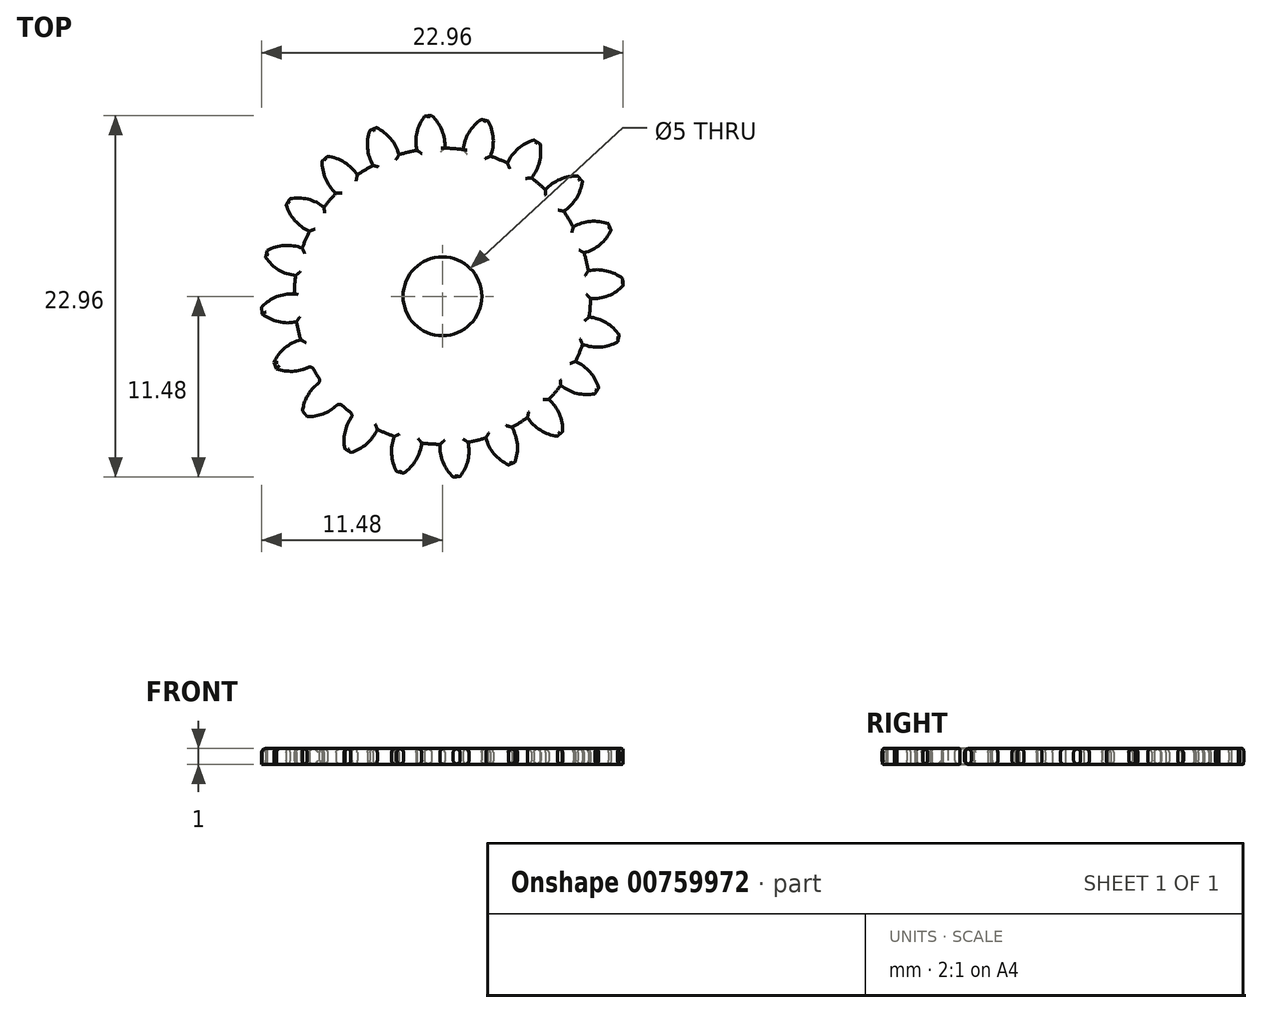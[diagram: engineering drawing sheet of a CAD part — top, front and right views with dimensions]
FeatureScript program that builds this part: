
annotation { "Feature Type Name" : "Feature", "Feature Type Description" : "" }
export const myFeature = defineFeature(function(context is Context, id is Id, definition is map)
    precondition{}
    {
        {
            assignVariable(context, id + "F0", {"name" : "GearDepth", "anyValue" : 1});
        }
        {
            assignVariable(context, id + "F1", {"name" : "TeethFillet", "anyValue" : getVariable(context, 'GearDepth') * .25});
        }
        {
            var Q0;
            Q0=qCreatedBy(makeId("Top.planeOp"),FACE);
            var sketch = newSketch(context, id + "F2", { "sketchPlane" : qUnion([Q0])});
            skCircle(sketch, "E0", {"center": v(0, 0) * mm, "radius": 9.4 * mm});
            skCircle(sketch, "E1", {"center": v(0, 0) * mm, "radius": 10.45 * mm, "construction": true});
            skCircle(sketch, "E2", {"center": v(0, 0) * mm, "radius": 11.5 * mm, "construction": true});
            skLineSegment(sketch, "E3", {"start": v(0, 0) * mm, "end": v(0, 17.6) * mm, "construction": true});
            skLineSegment(sketch, "E4", {"start": v(0, 0) * mm, "end": v(-1.42, 18) * mm, "construction": true});
            skLineSegment(sketch, "E5", {"start": v(0, 10.45) * mm, "end": v(-10.54, 10.45) * mm, "construction": true});
            skLineSegment(sketch, "E6", {"start": v(0, 10.45) * mm, "end": v(-10.3, 6.7) * mm, "construction": true});
            skCircle(sketch, "E7", {"center": v(0, 10.45) * mm, "radius": 2.61 * mm, "construction": true});
            skCircle(sketch, "E8", {"center": v(-2.46, 9.56) * mm, "radius": 2.61 * mm, "construction": true});
            skArc(sketch, "E9", {"start": v(-4.91, 10.45) * mm, "mid": v(-4.92, 10.42) * mm, "end": v(-4.94, 10.39) * mm});
            skArc(sketch, "E10.trimOffspring", {"start": v(0.15, 9.4) * mm, "mid": v(-0.03, 10.54) * mm, "end": v(-0.68, 11.48) * mm});
            skArc(sketch, "E11.MirrorCS", {"start": v(-1.62, 9.27) * mm, "mid": v(-1.62, 10.41) * mm, "end": v(-1.12, 11.45) * mm});
            skLineSegment(sketch, "E12", {"start": v(-1.12, 11.45) * mm, "end": v(-0.68, 11.48) * mm});
            skArc(sketch, "E13.1.0", {"start": v(-2.76, 9) * mm, "mid": v(-3.29, 10.01) * mm, "end": v(-4.2, 10.7) * mm});
            skLineSegment(sketch, "E13.1.1", {"start": v(-4.6, 10.54) * mm, "end": v(-4.2, 10.7) * mm});
            skArc(sketch, "E13.1.2", {"start": v(-4.4, 8.31) * mm, "mid": v(-4.76, 9.4) * mm, "end": v(-4.6, 10.54) * mm});
            skArc(sketch, "E13.2.0", {"start": v(-5.4, 7.7) * mm, "mid": v(-6.22, 8.5) * mm, "end": v(-7.3, 8.89) * mm});
            skLineSegment(sketch, "E13.2.1", {"start": v(-7.64, 8.6) * mm, "end": v(-7.3, 8.89) * mm});
            skArc(sketch, "E13.2.2", {"start": v(-6.76, 6.54) * mm, "mid": v(-7.43, 7.47) * mm, "end": v(-7.64, 8.6) * mm});
            skArc(sketch, "E13.3.0", {"start": v(-7.52, 5.65) * mm, "mid": v(-8.54, 6.17) * mm, "end": v(-9.69, 6.2) * mm});
            skLineSegment(sketch, "E13.3.1", {"start": v(-9.92, 5.82) * mm, "end": v(-9.69, 6.2) * mm});
            skArc(sketch, "E13.3.2", {"start": v(-8.45, 4.13) * mm, "mid": v(-9.37, 4.81) * mm, "end": v(-9.92, 5.82) * mm});
            skArc(sketch, "E13.4.0", {"start": v(-8.9, 3.05) * mm, "mid": v(-10.03, 3.23) * mm, "end": v(-11.13, 2.9) * mm});
            skLineSegment(sketch, "E13.4.1", {"start": v(-11.23, 2.47) * mm, "end": v(-11.13, 2.9) * mm});
            skArc(sketch, "E13.4.2", {"start": v(-9.32, 1.32) * mm, "mid": v(-10.4, 1.68) * mm, "end": v(-11.23, 2.47) * mm});
            skArc(sketch, "E13.5.0", {"start": v(-9.4, 0.15) * mm, "mid": v(-10.54, -0.03) * mm, "end": v(-11.48, -0.68) * mm});
            skLineSegment(sketch, "E13.5.1", {"start": v(-11.45, -1.12) * mm, "end": v(-11.48, -0.68) * mm});
            skArc(sketch, "E13.5.2", {"start": v(-9.27, -1.62) * mm, "mid": v(-10.41, -1.62) * mm, "end": v(-11.45, -1.12) * mm});
            skArc(sketch, "E13.6.0", {"start": v(-9, -2.76) * mm, "mid": v(-10.01, -3.29) * mm, "end": v(-10.7, -4.2) * mm});
            skLineSegment(sketch, "E13.6.1", {"start": v(-10.54, -4.6) * mm, "end": v(-10.7, -4.2) * mm});
            skArc(sketch, "E13.6.2", {"start": v(-8.31, -4.4) * mm, "mid": v(-9.4, -4.76) * mm, "end": v(-10.54, -4.6) * mm});
            skArc(sketch, "E13.7.0", {"start": v(-7.7, -5.4) * mm, "mid": v(-8.5, -6.22) * mm, "end": v(-8.89, -7.3) * mm});
            skLineSegment(sketch, "E13.7.1", {"start": v(-8.6, -7.64) * mm, "end": v(-8.89, -7.3) * mm});
            skArc(sketch, "E13.7.2", {"start": v(-6.54, -6.76) * mm, "mid": v(-7.47, -7.43) * mm, "end": v(-8.6, -7.64) * mm});
            skArc(sketch, "E13.8.0", {"start": v(-5.65, -7.52) * mm, "mid": v(-6.17, -8.54) * mm, "end": v(-6.2, -9.69) * mm});
            skLineSegment(sketch, "E13.8.1", {"start": v(-5.82, -9.92) * mm, "end": v(-6.2, -9.69) * mm});
            skArc(sketch, "E13.8.2", {"start": v(-4.13, -8.45) * mm, "mid": v(-4.81, -9.37) * mm, "end": v(-5.82, -9.92) * mm});
            skArc(sketch, "E13.9.0", {"start": v(-3.05, -8.9) * mm, "mid": v(-3.23, -10.03) * mm, "end": v(-2.9, -11.13) * mm});
            skLineSegment(sketch, "E13.9.1", {"start": v(-2.47, -11.23) * mm, "end": v(-2.9, -11.13) * mm});
            skArc(sketch, "E13.9.2", {"start": v(-1.32, -9.32) * mm, "mid": v(-1.68, -10.4) * mm, "end": v(-2.47, -11.23) * mm});
            skArc(sketch, "E13.10.0", {"start": v(-0.15, -9.4) * mm, "mid": v(0.03, -10.54) * mm, "end": v(0.68, -11.48) * mm});
            skLineSegment(sketch, "E13.10.1", {"start": v(1.12, -11.45) * mm, "end": v(0.68, -11.48) * mm});
            skArc(sketch, "E13.10.2", {"start": v(1.62, -9.27) * mm, "mid": v(1.62, -10.41) * mm, "end": v(1.12, -11.45) * mm});
            skArc(sketch, "E13.11.0", {"start": v(2.76, -9) * mm, "mid": v(3.29, -10.01) * mm, "end": v(4.2, -10.7) * mm});
            skLineSegment(sketch, "E13.11.1", {"start": v(4.6, -10.54) * mm, "end": v(4.2, -10.7) * mm});
            skArc(sketch, "E13.11.2", {"start": v(4.4, -8.31) * mm, "mid": v(4.76, -9.4) * mm, "end": v(4.6, -10.54) * mm});
            skArc(sketch, "E13.12.0", {"start": v(5.4, -7.7) * mm, "mid": v(6.22, -8.5) * mm, "end": v(7.3, -8.89) * mm});
            skLineSegment(sketch, "E13.12.1", {"start": v(7.64, -8.6) * mm, "end": v(7.3, -8.89) * mm});
            skArc(sketch, "E13.12.2", {"start": v(6.76, -6.54) * mm, "mid": v(7.43, -7.47) * mm, "end": v(7.64, -8.6) * mm});
            skArc(sketch, "E13.13.0", {"start": v(7.52, -5.65) * mm, "mid": v(8.54, -6.17) * mm, "end": v(9.69, -6.2) * mm});
            skLineSegment(sketch, "E13.13.1", {"start": v(9.92, -5.82) * mm, "end": v(9.69, -6.2) * mm});
            skArc(sketch, "E13.13.2", {"start": v(8.45, -4.13) * mm, "mid": v(9.37, -4.81) * mm, "end": v(9.92, -5.82) * mm});
            skArc(sketch, "E13.14.0", {"start": v(8.9, -3.05) * mm, "mid": v(10.03, -3.23) * mm, "end": v(11.13, -2.9) * mm});
            skLineSegment(sketch, "E13.14.1", {"start": v(11.23, -2.47) * mm, "end": v(11.13, -2.9) * mm});
            skArc(sketch, "E13.14.2", {"start": v(9.32, -1.32) * mm, "mid": v(10.4, -1.68) * mm, "end": v(11.23, -2.47) * mm});
            skArc(sketch, "E13.15.0", {"start": v(9.4, -0.15) * mm, "mid": v(10.54, 0.03) * mm, "end": v(11.48, 0.68) * mm});
            skLineSegment(sketch, "E13.15.1", {"start": v(11.45, 1.12) * mm, "end": v(11.48, 0.68) * mm});
            skArc(sketch, "E13.15.2", {"start": v(9.27, 1.62) * mm, "mid": v(10.41, 1.62) * mm, "end": v(11.45, 1.12) * mm});
            skArc(sketch, "E13.16.0", {"start": v(9, 2.76) * mm, "mid": v(10.01, 3.29) * mm, "end": v(10.7, 4.2) * mm});
            skLineSegment(sketch, "E13.16.1", {"start": v(10.54, 4.6) * mm, "end": v(10.7, 4.2) * mm});
            skArc(sketch, "E13.16.2", {"start": v(8.31, 4.4) * mm, "mid": v(9.4, 4.76) * mm, "end": v(10.54, 4.6) * mm});
            skArc(sketch, "E13.17.0", {"start": v(7.7, 5.4) * mm, "mid": v(8.5, 6.22) * mm, "end": v(8.89, 7.3) * mm});
            skLineSegment(sketch, "E13.17.1", {"start": v(8.6, 7.64) * mm, "end": v(8.89, 7.3) * mm});
            skArc(sketch, "E13.17.2", {"start": v(6.54, 6.76) * mm, "mid": v(7.47, 7.43) * mm, "end": v(8.6, 7.64) * mm});
            skArc(sketch, "E13.18.0", {"start": v(5.65, 7.52) * mm, "mid": v(6.17, 8.54) * mm, "end": v(6.2, 9.69) * mm});
            skLineSegment(sketch, "E13.18.1", {"start": v(5.82, 9.92) * mm, "end": v(6.2, 9.69) * mm});
            skArc(sketch, "E13.18.2", {"start": v(4.13, 8.45) * mm, "mid": v(4.81, 9.37) * mm, "end": v(5.82, 9.92) * mm});
            skArc(sketch, "E13.19.0", {"start": v(3.05, 8.9) * mm, "mid": v(3.23, 10.03) * mm, "end": v(2.9, 11.13) * mm});
            skLineSegment(sketch, "E13.19.1", {"start": v(2.47, 11.23) * mm, "end": v(2.9, 11.13) * mm});
            skArc(sketch, "E13.19.2", {"start": v(1.32, 9.32) * mm, "mid": v(1.68, 10.4) * mm, "end": v(2.47, 11.23) * mm});
            skCircle(sketch, "E14", {"center": v(0, 0) * mm, "radius": 2.5 * mm});
            skSolve(sketch);
        }
        {
            var Q0;
            {var subQ0=sQuery(id+"F2.wireOp",EDGE,"E10.trimOffspring");Q0=makeQuery(id+"F2.imprint","IMPRINT",FACE,{"disambiguationData":[TD([[makeQuery(id+"F2.imprint","IMPRINT",EDGE,{"derivedFrom":subQ0}),1.0]])]});}
            var Q1;
            {var subQ0=sQuery(id+"F2.wireOp",EDGE,"E0");var subQ1=makeQuery(id+"F2.imprint","INTERSECT",VERTEX,{"derivedFrom":[subQ0,sQuery(id+"F2.wireOp",EDGE,"E10.trimOffspring")]});Q1=makeQuery(id+"F2.imprint","IMPRINT",FACE,{"disambiguationData":[TD([[makeQuery(id+"F2.imprint","IMPRINT",EDGE,{"disambiguationData":[TD([[subQ1,-1.0]])],"derivedFrom":subQ0}),1.0]])]});}
            var Q2;
            {var subQ0=sQuery(id+"F2.wireOp",EDGE,"E13.1.0");Q2=makeQuery(id+"F2.imprint","IMPRINT",FACE,{"disambiguationData":[TD([[makeQuery(id+"F2.imprint","IMPRINT",EDGE,{"derivedFrom":subQ0}),1.0]])]});}
            var Q3;
            {var subQ0=sQuery(id+"F2.wireOp",EDGE,"E13.2.0");Q3=makeQuery(id+"F2.imprint","IMPRINT",FACE,{"disambiguationData":[TD([[makeQuery(id+"F2.imprint","IMPRINT",EDGE,{"derivedFrom":subQ0}),1.0]])]});}
            var Q4;
            {var subQ0=sQuery(id+"F2.wireOp",EDGE,"E13.3.0");Q4=makeQuery(id+"F2.imprint","IMPRINT",FACE,{"disambiguationData":[TD([[makeQuery(id+"F2.imprint","IMPRINT",EDGE,{"derivedFrom":subQ0}),1.0]])]});}
            var Q5;
            {var subQ0=sQuery(id+"F2.wireOp",EDGE,"E13.4.0");Q5=makeQuery(id+"F2.imprint","IMPRINT",FACE,{"disambiguationData":[TD([[makeQuery(id+"F2.imprint","IMPRINT",EDGE,{"derivedFrom":subQ0}),1.0]])]});}
            var Q6;
            {var subQ0=sQuery(id+"F2.wireOp",EDGE,"E13.5.0");Q6=makeQuery(id+"F2.imprint","IMPRINT",FACE,{"disambiguationData":[TD([[makeQuery(id+"F2.imprint","IMPRINT",EDGE,{"derivedFrom":subQ0}),1.0]])]});}
            var Q7;
            {var subQ0=sQuery(id+"F2.wireOp",EDGE,"E13.6.0");Q7=makeQuery(id+"F2.imprint","IMPRINT",FACE,{"disambiguationData":[TD([[makeQuery(id+"F2.imprint","IMPRINT",EDGE,{"derivedFrom":subQ0}),1.0]])]});}
            var Q8;
            {var subQ0=sQuery(id+"F2.wireOp",EDGE,"E13.7.0");Q8=makeQuery(id+"F2.imprint","IMPRINT",FACE,{"disambiguationData":[TD([[makeQuery(id+"F2.imprint","IMPRINT",EDGE,{"derivedFrom":subQ0}),1.0]])]});}
            var Q9;
            {var subQ0=sQuery(id+"F2.wireOp",EDGE,"E13.8.0");Q9=makeQuery(id+"F2.imprint","IMPRINT",FACE,{"disambiguationData":[TD([[makeQuery(id+"F2.imprint","IMPRINT",EDGE,{"derivedFrom":subQ0}),1.0]])]});}
            var Q10;
            {var subQ0=sQuery(id+"F2.wireOp",EDGE,"E13.9.0");Q10=makeQuery(id+"F2.imprint","IMPRINT",FACE,{"disambiguationData":[TD([[makeQuery(id+"F2.imprint","IMPRINT",EDGE,{"derivedFrom":subQ0}),1.0]])]});}
            var Q11;
            {var subQ0=sQuery(id+"F2.wireOp",EDGE,"E13.10.0");Q11=makeQuery(id+"F2.imprint","IMPRINT",FACE,{"disambiguationData":[TD([[makeQuery(id+"F2.imprint","IMPRINT",EDGE,{"derivedFrom":subQ0}),1.0]])]});}
            var Q12;
            {var subQ0=sQuery(id+"F2.wireOp",EDGE,"E13.11.0");Q12=makeQuery(id+"F2.imprint","IMPRINT",FACE,{"disambiguationData":[TD([[makeQuery(id+"F2.imprint","IMPRINT",EDGE,{"derivedFrom":subQ0}),1.0]])]});}
            var Q13;
            {var subQ0=sQuery(id+"F2.wireOp",EDGE,"E13.12.0");Q13=makeQuery(id+"F2.imprint","IMPRINT",FACE,{"disambiguationData":[TD([[makeQuery(id+"F2.imprint","IMPRINT",EDGE,{"derivedFrom":subQ0}),1.0]])]});}
            var Q14;
            {var subQ0=sQuery(id+"F2.wireOp",EDGE,"E13.13.0");Q14=makeQuery(id+"F2.imprint","IMPRINT",FACE,{"disambiguationData":[TD([[makeQuery(id+"F2.imprint","IMPRINT",EDGE,{"derivedFrom":subQ0}),1.0]])]});}
            var Q15;
            {var subQ0=sQuery(id+"F2.wireOp",EDGE,"E13.14.0");Q15=makeQuery(id+"F2.imprint","IMPRINT",FACE,{"disambiguationData":[TD([[makeQuery(id+"F2.imprint","IMPRINT",EDGE,{"derivedFrom":subQ0}),1.0]])]});}
            var Q16;
            {var subQ0=sQuery(id+"F2.wireOp",EDGE,"E13.15.0");Q16=makeQuery(id+"F2.imprint","IMPRINT",FACE,{"disambiguationData":[TD([[makeQuery(id+"F2.imprint","IMPRINT",EDGE,{"derivedFrom":subQ0}),1.0]])]});}
            var Q17;
            {var subQ0=sQuery(id+"F2.wireOp",EDGE,"E13.16.0");Q17=makeQuery(id+"F2.imprint","IMPRINT",FACE,{"disambiguationData":[TD([[makeQuery(id+"F2.imprint","IMPRINT",EDGE,{"derivedFrom":subQ0}),1.0]])]});}
            var Q18;
            {var subQ0=sQuery(id+"F2.wireOp",EDGE,"E13.17.0");Q18=makeQuery(id+"F2.imprint","IMPRINT",FACE,{"disambiguationData":[TD([[makeQuery(id+"F2.imprint","IMPRINT",EDGE,{"derivedFrom":subQ0}),1.0]])]});}
            var Q19;
            {var subQ0=sQuery(id+"F2.wireOp",EDGE,"E13.18.0");Q19=makeQuery(id+"F2.imprint","IMPRINT",FACE,{"disambiguationData":[TD([[makeQuery(id+"F2.imprint","IMPRINT",EDGE,{"derivedFrom":subQ0}),1.0]])]});}
            var Q20;
            {var subQ0=sQuery(id+"F2.wireOp",EDGE,"E13.19.0");Q20=makeQuery(id+"F2.imprint","IMPRINT",FACE,{"disambiguationData":[TD([[makeQuery(id+"F2.imprint","IMPRINT",EDGE,{"derivedFrom":subQ0}),1.0]])]});}
            var Q21;
            Q21=sQuery(id+"F2.wireOp",EDGE,"E0");
            var Q22;
            Q22=sQuery(id+"F2.wireOp",EDGE,"E10.trimOffspring");
            var Q23;
            Q23=sQuery(id+"F2.wireOp",EDGE,"E12");
            var Q24;
            Q24=sQuery(id+"F2.wireOp",EDGE,"E11.MirrorCS");
            extrude(context, id + "F3", {"entities" : qUnion([Q0, Q1, Q2, Q3, Q4, Q5, Q6, Q7, Q8, Q9, Q10, Q11, Q12, Q13, Q14, Q15, Q16, Q17, Q18, Q19, Q20]), "surfaceEntities" : qUnion([Q21, Q22, Q23, Q24]), "depth" : (getVariable(context, 'GearDepth')) * mm, "offsetDistance" : 25 * mm});
        }
        {
            var Q0;
            Q0=makeQuery(id+"F3.opExtrude","CAP_EDGE",EDGE,{"disambiguationData":[OSD([sQuery(id+"F2.wireOp",EDGE,"E13.5.2")])],"isStart":false});
            var Q1;
            Q1=makeQuery(id+"F3.opExtrude","CAP_EDGE",EDGE,{"disambiguationData":[OSD([sQuery(id+"F2.wireOp",EDGE,"E13.5.1")])],"isStart":false});
            var Q2;
            {var subQ0=sQuery(id+"F2.wireOp",EDGE,"E0");Q2=makeQuery(id+"F3.opExtrude","CAP_EDGE",EDGE,{"disambiguationData":[OSD([subQ0]),TDD([makeQuery(id+"F2.imprint","IMPRINT",EDGE,{"disambiguationData":[TD([[makeQuery(id+"F2.imprint","INTERSECT",VERTEX,{"derivedFrom":[subQ0,sQuery(id+"F2.wireOp",EDGE,"E13.5.2")]}),-1.0]])],"derivedFrom":subQ0})])],"isStart":false});}
            var Q3;
            Q3=makeQuery(id+"F3.opExtrude","CAP_EDGE",EDGE,{"disambiguationData":[OSD([sQuery(id+"F2.wireOp",EDGE,"E13.6.0")])],"isStart":false});
            var Q4;
            Q4=makeQuery(id+"F3.opExtrude","CAP_EDGE",EDGE,{"disambiguationData":[OSD([sQuery(id+"F2.wireOp",EDGE,"E13.6.1")])],"isStart":false});
            var Q5;
            Q5=makeQuery(id+"F3.opExtrude","CAP_EDGE",EDGE,{"disambiguationData":[OSD([sQuery(id+"F2.wireOp",EDGE,"E13.6.2")])],"isStart":false});
            var Q6;
            {var subQ0=sQuery(id+"F2.wireOp",EDGE,"E0");Q6=makeQuery(id+"F3.opExtrude","SWEPT_FACE",FACE,{"disambiguationData":[OSD([subQ0]),TDD([makeQuery(id+"F2.imprint","IMPRINT",EDGE,{"disambiguationData":[TD([[makeQuery(id+"F2.imprint","INTERSECT",VERTEX,{"derivedFrom":[subQ0,sQuery(id+"F2.wireOp",EDGE,"E13.6.2")]}),-1.0]])],"derivedFrom":subQ0})])]});}
            var Q7;
            {var subQ0=sQuery(id+"F2.wireOp",EDGE,"E0");Q7=makeQuery(id+"F3.opExtrude","CAP_EDGE",EDGE,{"disambiguationData":[OSD([subQ0]),TDD([makeQuery(id+"F2.imprint","IMPRINT",EDGE,{"disambiguationData":[TD([[makeQuery(id+"F2.imprint","INTERSECT",VERTEX,{"derivedFrom":[subQ0,sQuery(id+"F2.wireOp",EDGE,"E13.6.2")]}),-1.0]])],"derivedFrom":subQ0})])],"isStart":false});}
            var Q8;
            Q8=makeQuery(id+"F3.opExtrude","CAP_EDGE",EDGE,{"disambiguationData":[OSD([sQuery(id+"F2.wireOp",EDGE,"E13.7.2")])],"isStart":true});
            var Q9;
            {var subQ0=sQuery(id+"F2.wireOp",EDGE,"E0");Q9=makeQuery(id+"F3.opExtrude","CAP_EDGE",EDGE,{"disambiguationData":[OSD([subQ0]),TDD([makeQuery(id+"F2.imprint","IMPRINT",EDGE,{"disambiguationData":[TD([[makeQuery(id+"F2.imprint","INTERSECT",VERTEX,{"derivedFrom":[subQ0,sQuery(id+"F2.wireOp",EDGE,"E13.7.2")]}),-1.0]])],"derivedFrom":subQ0})])],"isStart":true});}
            var Q10;
            Q10=makeQuery(id+"F3.opExtrude","CAP_EDGE",EDGE,{"disambiguationData":[OSD([sQuery(id+"F2.wireOp",EDGE,"E13.7.2")])],"isStart":false});
            var Q11;
            {var subQ0=sQuery(id+"F2.wireOp",EDGE,"E0");Q11=makeQuery(id+"F3.opExtrude","CAP_EDGE",EDGE,{"disambiguationData":[OSD([subQ0]),TDD([makeQuery(id+"F2.imprint","IMPRINT",EDGE,{"disambiguationData":[TD([[makeQuery(id+"F2.imprint","INTERSECT",VERTEX,{"derivedFrom":[subQ0,sQuery(id+"F2.wireOp",EDGE,"E13.7.2")]}),-1.0]])],"derivedFrom":subQ0})])],"isStart":false});}
            var Q12;
            Q12=makeQuery(id+"F3.opExtrude","CAP_EDGE",EDGE,{"disambiguationData":[OSD([sQuery(id+"F2.wireOp",EDGE,"E13.8.0")])],"isStart":false});
            var Q13;
            {var subQ0=sQuery(id+"F2.wireOp",EDGE,"E0");Q13=makeQuery(id+"F3.opExtrude","SWEPT_FACE",FACE,{"disambiguationData":[OSD([subQ0]),TDD([makeQuery(id+"F2.imprint","IMPRINT",EDGE,{"disambiguationData":[TD([[makeQuery(id+"F2.imprint","INTERSECT",VERTEX,{"derivedFrom":[subQ0,sQuery(id+"F2.wireOp",EDGE,"E13.7.2")]}),-1.0]])],"derivedFrom":subQ0})])]});}
            var Q14;
            Q14=makeQuery(id+"F3.opExtrude","CAP_EDGE",EDGE,{"disambiguationData":[OSD([sQuery(id+"F2.wireOp",EDGE,"E13.6.0")])],"isStart":true});
            var Q15;
            Q15=makeQuery(id+"F3.opExtrude","CAP_EDGE",EDGE,{"disambiguationData":[OSD([sQuery(id+"F2.wireOp",EDGE,"E13.8.2")])],"isStart":false});
            var Q16;
            {var subQ0=sQuery(id+"F2.wireOp",EDGE,"E0");Q16=makeQuery(id+"F3.opExtrude","CAP_EDGE",EDGE,{"disambiguationData":[OSD([subQ0]),TDD([makeQuery(id+"F2.imprint","IMPRINT",EDGE,{"disambiguationData":[TD([[makeQuery(id+"F2.imprint","INTERSECT",VERTEX,{"derivedFrom":[subQ0,sQuery(id+"F2.wireOp",EDGE,"E13.8.2")]}),-1.0]])],"derivedFrom":subQ0})])],"isStart":false});}
            var Q17;
            Q17=makeQuery(id+"F3.opExtrude","CAP_EDGE",EDGE,{"disambiguationData":[OSD([sQuery(id+"F2.wireOp",EDGE,"E13.9.0")])],"isStart":false});
            var Q18;
            Q18=makeQuery(id+"F3.opExtrude","CAP_EDGE",EDGE,{"disambiguationData":[OSD([sQuery(id+"F2.wireOp",EDGE,"E13.9.2")])],"isStart":false});
            var Q19;
            {var subQ0=sQuery(id+"F2.wireOp",EDGE,"E0");Q19=makeQuery(id+"F3.opExtrude","CAP_EDGE",EDGE,{"disambiguationData":[OSD([subQ0]),TDD([makeQuery(id+"F2.imprint","IMPRINT",EDGE,{"disambiguationData":[TD([[makeQuery(id+"F2.imprint","INTERSECT",VERTEX,{"derivedFrom":[subQ0,sQuery(id+"F2.wireOp",EDGE,"E13.9.2")]}),-1.0]])],"derivedFrom":subQ0})])],"isStart":false});}
            var Q20;
            Q20=makeQuery(id+"F3.opExtrude","CAP_EDGE",EDGE,{"disambiguationData":[OSD([sQuery(id+"F2.wireOp",EDGE,"E13.10.0")])],"isStart":false});
            var Q21;
            Q21=makeQuery(id+"F3.opExtrude","CAP_EDGE",EDGE,{"disambiguationData":[OSD([sQuery(id+"F2.wireOp",EDGE,"E13.10.2")])],"isStart":false});
            var Q22;
            {var subQ0=sQuery(id+"F2.wireOp",EDGE,"E0");Q22=makeQuery(id+"F3.opExtrude","CAP_EDGE",EDGE,{"disambiguationData":[OSD([subQ0]),TDD([makeQuery(id+"F2.imprint","IMPRINT",EDGE,{"disambiguationData":[TD([[makeQuery(id+"F2.imprint","INTERSECT",VERTEX,{"derivedFrom":[subQ0,sQuery(id+"F2.wireOp",EDGE,"E13.10.2")]}),-1.0]])],"derivedFrom":subQ0})])],"isStart":false});}
            var Q23;
            Q23=makeQuery(id+"F3.opExtrude","CAP_EDGE",EDGE,{"disambiguationData":[OSD([sQuery(id+"F2.wireOp",EDGE,"E13.11.0")])],"isStart":false});
            var Q24;
            Q24=makeQuery(id+"F3.opExtrude","CAP_EDGE",EDGE,{"disambiguationData":[OSD([sQuery(id+"F2.wireOp",EDGE,"E13.11.2")])],"isStart":false});
            var Q25;
            {var subQ0=sQuery(id+"F2.wireOp",EDGE,"E0");Q25=makeQuery(id+"F3.opExtrude","CAP_EDGE",EDGE,{"disambiguationData":[OSD([subQ0]),TDD([makeQuery(id+"F2.imprint","IMPRINT",EDGE,{"disambiguationData":[TD([[makeQuery(id+"F2.imprint","INTERSECT",VERTEX,{"derivedFrom":[subQ0,sQuery(id+"F2.wireOp",EDGE,"E13.11.2")]}),-1.0]])],"derivedFrom":subQ0})])],"isStart":false});}
            var Q26;
            Q26=makeQuery(id+"F3.opExtrude","CAP_EDGE",EDGE,{"disambiguationData":[OSD([sQuery(id+"F2.wireOp",EDGE,"E13.12.0")])],"isStart":false});
            var Q27;
            Q27=makeQuery(id+"F3.opExtrude","CAP_EDGE",EDGE,{"disambiguationData":[OSD([sQuery(id+"F2.wireOp",EDGE,"E13.12.2")])],"isStart":false});
            var Q28;
            {var subQ0=sQuery(id+"F2.wireOp",EDGE,"E0");Q28=makeQuery(id+"F3.opExtrude","CAP_EDGE",EDGE,{"disambiguationData":[OSD([subQ0]),TDD([makeQuery(id+"F2.imprint","IMPRINT",EDGE,{"disambiguationData":[TD([[makeQuery(id+"F2.imprint","INTERSECT",VERTEX,{"derivedFrom":[subQ0,sQuery(id+"F2.wireOp",EDGE,"E13.12.2")]}),-1.0]])],"derivedFrom":subQ0})])],"isStart":false});}
            var Q29;
            Q29=makeQuery(id+"F3.opExtrude","CAP_EDGE",EDGE,{"disambiguationData":[OSD([sQuery(id+"F2.wireOp",EDGE,"E13.13.0")])],"isStart":false});
            var Q30;
            Q30=makeQuery(id+"F3.opExtrude","CAP_EDGE",EDGE,{"disambiguationData":[OSD([sQuery(id+"F2.wireOp",EDGE,"E13.13.2")])],"isStart":false});
            var Q31;
            {var subQ0=sQuery(id+"F2.wireOp",EDGE,"E0");Q31=makeQuery(id+"F3.opExtrude","CAP_EDGE",EDGE,{"disambiguationData":[OSD([subQ0]),TDD([makeQuery(id+"F2.imprint","IMPRINT",EDGE,{"disambiguationData":[TD([[makeQuery(id+"F2.imprint","INTERSECT",VERTEX,{"derivedFrom":[subQ0,sQuery(id+"F2.wireOp",EDGE,"E13.13.2")]}),-1.0]])],"derivedFrom":subQ0})])],"isStart":false});}
            var Q32;
            Q32=makeQuery(id+"F3.opExtrude","CAP_EDGE",EDGE,{"disambiguationData":[OSD([sQuery(id+"F2.wireOp",EDGE,"E13.14.0")])],"isStart":false});
            var Q33;
            Q33=makeQuery(id+"F3.opExtrude","CAP_EDGE",EDGE,{"disambiguationData":[OSD([sQuery(id+"F2.wireOp",EDGE,"E13.14.2")])],"isStart":false});
            var Q34;
            {var subQ0=sQuery(id+"F2.wireOp",EDGE,"E0");Q34=makeQuery(id+"F3.opExtrude","CAP_EDGE",EDGE,{"disambiguationData":[OSD([subQ0]),TDD([makeQuery(id+"F2.imprint","IMPRINT",EDGE,{"disambiguationData":[TD([[makeQuery(id+"F2.imprint","INTERSECT",VERTEX,{"derivedFrom":[subQ0,sQuery(id+"F2.wireOp",EDGE,"E13.14.2")]}),-1.0]])],"derivedFrom":subQ0})])],"isStart":false});}
            var Q35;
            Q35=makeQuery(id+"F3.opExtrude","CAP_EDGE",EDGE,{"disambiguationData":[OSD([sQuery(id+"F2.wireOp",EDGE,"E13.15.0")])],"isStart":false});
            var Q36;
            {var subQ0=sQuery(id+"F2.wireOp",EDGE,"E0");Q36=makeQuery(id+"F3.opExtrude","CAP_EDGE",EDGE,{"disambiguationData":[OSD([subQ0]),TDD([makeQuery(id+"F2.imprint","IMPRINT",EDGE,{"disambiguationData":[TD([[makeQuery(id+"F2.imprint","INTERSECT",VERTEX,{"derivedFrom":[subQ0,sQuery(id+"F2.wireOp",EDGE,"E13.14.2")]}),-1.0]])],"derivedFrom":subQ0})])],"isStart":false});}
            var Q37;
            Q37=makeQuery(id+"F3.opExtrude","CAP_EDGE",EDGE,{"disambiguationData":[OSD([sQuery(id+"F2.wireOp",EDGE,"E13.15.2")])],"isStart":false});
            var Q38;
            {var subQ0=sQuery(id+"F2.wireOp",EDGE,"E0");Q38=makeQuery(id+"F3.opExtrude","CAP_EDGE",EDGE,{"disambiguationData":[OSD([subQ0]),TDD([makeQuery(id+"F2.imprint","IMPRINT",EDGE,{"disambiguationData":[TD([[makeQuery(id+"F2.imprint","INTERSECT",VERTEX,{"derivedFrom":[subQ0,sQuery(id+"F2.wireOp",EDGE,"E13.15.2")]}),-1.0]])],"derivedFrom":subQ0})])],"isStart":false});}
            var Q39;
            Q39=makeQuery(id+"F3.opExtrude","CAP_EDGE",EDGE,{"disambiguationData":[OSD([sQuery(id+"F2.wireOp",EDGE,"E13.16.0")])],"isStart":false});
            var Q40;
            Q40=makeQuery(id+"F3.opExtrude","CAP_EDGE",EDGE,{"disambiguationData":[OSD([sQuery(id+"F2.wireOp",EDGE,"E13.16.2")])],"isStart":false});
            var Q41;
            Q41=makeQuery(id+"F3.opExtrude","CAP_EDGE",EDGE,{"disambiguationData":[OSD([sQuery(id+"F2.wireOp",EDGE,"E13.17.0")])],"isStart":false});
            var Q42;
            {var subQ0=sQuery(id+"F2.wireOp",EDGE,"E0");Q42=makeQuery(id+"F3.opExtrude","CAP_EDGE",EDGE,{"disambiguationData":[OSD([subQ0]),TDD([makeQuery(id+"F2.imprint","IMPRINT",EDGE,{"disambiguationData":[TD([[makeQuery(id+"F2.imprint","INTERSECT",VERTEX,{"derivedFrom":[subQ0,sQuery(id+"F2.wireOp",EDGE,"E13.16.2")]}),-1.0]])],"derivedFrom":subQ0})])],"isStart":false});}
            var Q43;
            Q43=makeQuery(id+"F3.opExtrude","CAP_EDGE",EDGE,{"disambiguationData":[OSD([sQuery(id+"F2.wireOp",EDGE,"E13.17.2")])],"isStart":false});
            var Q44;
            {var subQ0=sQuery(id+"F2.wireOp",EDGE,"E0");Q44=makeQuery(id+"F3.opExtrude","CAP_EDGE",EDGE,{"disambiguationData":[OSD([subQ0]),TDD([makeQuery(id+"F2.imprint","IMPRINT",EDGE,{"disambiguationData":[TD([[makeQuery(id+"F2.imprint","INTERSECT",VERTEX,{"derivedFrom":[subQ0,sQuery(id+"F2.wireOp",EDGE,"E13.17.2")]}),-1.0]])],"derivedFrom":subQ0})])],"isStart":false});}
            var Q45;
            Q45=makeQuery(id+"F3.opExtrude","CAP_EDGE",EDGE,{"disambiguationData":[OSD([sQuery(id+"F2.wireOp",EDGE,"E13.18.0")])],"isStart":false});
            var Q46;
            Q46=makeQuery(id+"F3.opExtrude","CAP_EDGE",EDGE,{"disambiguationData":[OSD([sQuery(id+"F2.wireOp",EDGE,"E13.18.2")])],"isStart":false});
            var Q47;
            {var subQ0=sQuery(id+"F2.wireOp",EDGE,"E0");Q47=makeQuery(id+"F3.opExtrude","CAP_EDGE",EDGE,{"disambiguationData":[OSD([subQ0]),TDD([makeQuery(id+"F2.imprint","IMPRINT",EDGE,{"disambiguationData":[TD([[makeQuery(id+"F2.imprint","INTERSECT",VERTEX,{"derivedFrom":[subQ0,sQuery(id+"F2.wireOp",EDGE,"E13.18.2")]}),-1.0]])],"derivedFrom":subQ0})])],"isStart":false});}
            var Q48;
            Q48=makeQuery(id+"F3.opExtrude","CAP_EDGE",EDGE,{"disambiguationData":[OSD([sQuery(id+"F2.wireOp",EDGE,"E13.19.0")])],"isStart":false});
            var Q49;
            Q49=makeQuery(id+"F3.opExtrude","CAP_EDGE",EDGE,{"disambiguationData":[OSD([sQuery(id+"F2.wireOp",EDGE,"E13.19.2")])],"isStart":false});
            var Q50;
            Q50=makeQuery(id+"F3.opExtrude","CAP_EDGE",EDGE,{"disambiguationData":[OSD([sQuery(id+"F2.wireOp",EDGE,"E10.trimOffspring")])],"isStart":false});
            var Q51;
            Q51=makeQuery(id+"F3.opExtrude","CAP_EDGE",EDGE,{"disambiguationData":[OSD([sQuery(id+"F2.wireOp",EDGE,"E11.MirrorCS")])],"isStart":false});
            var Q52;
            {var subQ0=sQuery(id+"F2.wireOp",EDGE,"E0");Q52=makeQuery(id+"F3.opExtrude","CAP_EDGE",EDGE,{"disambiguationData":[OSD([subQ0]),TDD([makeQuery(id+"F2.imprint","IMPRINT",EDGE,{"disambiguationData":[TD([[makeQuery(id+"F2.imprint","INTERSECT",VERTEX,{"derivedFrom":[subQ0,sQuery(id+"F2.wireOp",EDGE,"E11.MirrorCS")]}),-1.0]])],"derivedFrom":subQ0})])],"isStart":false});}
            var Q53;
            Q53=makeQuery(id+"F3.opExtrude","CAP_EDGE",EDGE,{"disambiguationData":[OSD([sQuery(id+"F2.wireOp",EDGE,"E13.1.0")])],"isStart":false});
            var Q54;
            Q54=makeQuery(id+"F3.opExtrude","CAP_EDGE",EDGE,{"disambiguationData":[OSD([sQuery(id+"F2.wireOp",EDGE,"E13.1.2")])],"isStart":false});
            var Q55;
            {var subQ0=sQuery(id+"F2.wireOp",EDGE,"E0");Q55=makeQuery(id+"F3.opExtrude","CAP_EDGE",EDGE,{"disambiguationData":[OSD([subQ0]),TDD([makeQuery(id+"F2.imprint","IMPRINT",EDGE,{"disambiguationData":[TD([[makeQuery(id+"F2.imprint","INTERSECT",VERTEX,{"derivedFrom":[subQ0,sQuery(id+"F2.wireOp",EDGE,"E13.1.2")]}),-1.0]])],"derivedFrom":subQ0})])],"isStart":false});}
            var Q56;
            Q56=makeQuery(id+"F3.opExtrude","CAP_EDGE",EDGE,{"disambiguationData":[OSD([sQuery(id+"F2.wireOp",EDGE,"E13.2.0")])],"isStart":false});
            var Q57;
            Q57=makeQuery(id+"F3.opExtrude","CAP_EDGE",EDGE,{"disambiguationData":[OSD([sQuery(id+"F2.wireOp",EDGE,"E13.2.2")])],"isStart":false});
            var Q58;
            {var subQ0=sQuery(id+"F2.wireOp",EDGE,"E0");Q58=makeQuery(id+"F3.opExtrude","CAP_EDGE",EDGE,{"disambiguationData":[OSD([subQ0]),TDD([makeQuery(id+"F2.imprint","IMPRINT",EDGE,{"disambiguationData":[TD([[makeQuery(id+"F2.imprint","INTERSECT",VERTEX,{"derivedFrom":[subQ0,sQuery(id+"F2.wireOp",EDGE,"E13.2.2")]}),-1.0]])],"derivedFrom":subQ0})])],"isStart":false});}
            var Q59;
            Q59=makeQuery(id+"F3.opExtrude","CAP_EDGE",EDGE,{"disambiguationData":[OSD([sQuery(id+"F2.wireOp",EDGE,"E13.3.0")])],"isStart":false});
            var Q60;
            Q60=makeQuery(id+"F3.opExtrude","CAP_EDGE",EDGE,{"disambiguationData":[OSD([sQuery(id+"F2.wireOp",EDGE,"E13.3.2")])],"isStart":false});
            var Q61;
            {var subQ0=sQuery(id+"F2.wireOp",EDGE,"E0");Q61=makeQuery(id+"F3.opExtrude","CAP_EDGE",EDGE,{"disambiguationData":[OSD([subQ0]),TDD([makeQuery(id+"F2.imprint","IMPRINT",EDGE,{"disambiguationData":[TD([[makeQuery(id+"F2.imprint","INTERSECT",VERTEX,{"derivedFrom":[subQ0,sQuery(id+"F2.wireOp",EDGE,"E13.3.2")]}),-1.0]])],"derivedFrom":subQ0})])],"isStart":false});}
            var Q62;
            Q62=makeQuery(id+"F3.opExtrude","CAP_EDGE",EDGE,{"disambiguationData":[OSD([sQuery(id+"F2.wireOp",EDGE,"E13.4.0")])],"isStart":false});
            var Q63;
            Q63=makeQuery(id+"F3.opExtrude","CAP_EDGE",EDGE,{"disambiguationData":[OSD([sQuery(id+"F2.wireOp",EDGE,"E13.4.2")])],"isStart":false});
            var Q64;
            {var subQ0=sQuery(id+"F2.wireOp",EDGE,"E0");Q64=makeQuery(id+"F3.opExtrude","CAP_EDGE",EDGE,{"disambiguationData":[OSD([subQ0]),TDD([makeQuery(id+"F2.imprint","IMPRINT",EDGE,{"disambiguationData":[TD([[makeQuery(id+"F2.imprint","INTERSECT",VERTEX,{"derivedFrom":[subQ0,sQuery(id+"F2.wireOp",EDGE,"E13.4.2")]}),-1.0]])],"derivedFrom":subQ0})])],"isStart":false});}
            var Q65;
            {var subQ0=sQuery(id+"F2.wireOp",EDGE,"E0");Q65=makeQuery(id+"F3.opExtrude","CAP_EDGE",EDGE,{"disambiguationData":[OSD([subQ0]),TDD([makeQuery(id+"F2.imprint","IMPRINT",EDGE,{"disambiguationData":[TD([[makeQuery(id+"F2.imprint","INTERSECT",VERTEX,{"derivedFrom":[subQ0,sQuery(id+"F2.wireOp",EDGE,"E13.5.2")]}),-1.0]])],"derivedFrom":subQ0})])],"isStart":true});}
            var Q66;
            Q66=makeQuery(id+"F3.opExtrude","CAP_EDGE",EDGE,{"disambiguationData":[OSD([sQuery(id+"F2.wireOp",EDGE,"E13.5.2")])],"isStart":true});
            var Q67;
            {var subQ0=sQuery(id+"F2.wireOp",EDGE,"E0");Q67=makeQuery(id+"F3.opExtrude","CAP_EDGE",EDGE,{"disambiguationData":[OSD([subQ0]),TDD([makeQuery(id+"F2.imprint","IMPRINT",EDGE,{"disambiguationData":[TD([[makeQuery(id+"F2.imprint","INTERSECT",VERTEX,{"derivedFrom":[subQ0,sQuery(id+"F2.wireOp",EDGE,"E13.4.2")]}),-1.0]])],"derivedFrom":subQ0})])],"isStart":true});}
            var Q68;
            Q68=makeQuery(id+"F3.opExtrude","CAP_EDGE",EDGE,{"disambiguationData":[OSD([sQuery(id+"F2.wireOp",EDGE,"E13.4.2")])],"isStart":true});
            var Q69;
            Q69=makeQuery(id+"F3.opExtrude","CAP_EDGE",EDGE,{"disambiguationData":[OSD([sQuery(id+"F2.wireOp",EDGE,"E13.4.0")])],"isStart":true});
            var Q70;
            {var subQ0=sQuery(id+"F2.wireOp",EDGE,"E0");Q70=makeQuery(id+"F3.opExtrude","CAP_EDGE",EDGE,{"disambiguationData":[OSD([subQ0]),TDD([makeQuery(id+"F2.imprint","IMPRINT",EDGE,{"disambiguationData":[TD([[makeQuery(id+"F2.imprint","INTERSECT",VERTEX,{"derivedFrom":[subQ0,sQuery(id+"F2.wireOp",EDGE,"E13.3.2")]}),-1.0]])],"derivedFrom":subQ0})])],"isStart":true});}
            var Q71;
            Q71=makeQuery(id+"F3.opExtrude","CAP_EDGE",EDGE,{"disambiguationData":[OSD([sQuery(id+"F2.wireOp",EDGE,"E13.3.2")])],"isStart":true});
            var Q72;
            Q72=makeQuery(id+"F3.opExtrude","CAP_EDGE",EDGE,{"disambiguationData":[OSD([sQuery(id+"F2.wireOp",EDGE,"E13.3.0")])],"isStart":true});
            var Q73;
            {var subQ0=sQuery(id+"F2.wireOp",EDGE,"E0");Q73=makeQuery(id+"F3.opExtrude","CAP_EDGE",EDGE,{"disambiguationData":[OSD([subQ0]),TDD([makeQuery(id+"F2.imprint","IMPRINT",EDGE,{"disambiguationData":[TD([[makeQuery(id+"F2.imprint","INTERSECT",VERTEX,{"derivedFrom":[subQ0,sQuery(id+"F2.wireOp",EDGE,"E13.2.2")]}),-1.0]])],"derivedFrom":subQ0})])],"isStart":true});}
            var Q74;
            Q74=makeQuery(id+"F3.opExtrude","CAP_EDGE",EDGE,{"disambiguationData":[OSD([sQuery(id+"F2.wireOp",EDGE,"E13.2.2")])],"isStart":true});
            var Q75;
            Q75=makeQuery(id+"F3.opExtrude","CAP_EDGE",EDGE,{"disambiguationData":[OSD([sQuery(id+"F2.wireOp",EDGE,"E13.2.0")])],"isStart":true});
            var Q76;
            Q76=makeQuery(id+"F3.opExtrude","CAP_EDGE",EDGE,{"disambiguationData":[OSD([sQuery(id+"F2.wireOp",EDGE,"E13.1.2")])],"isStart":true});
            var Q77;
            {var subQ0=sQuery(id+"F2.wireOp",EDGE,"E0");Q77=makeQuery(id+"F3.opExtrude","CAP_EDGE",EDGE,{"disambiguationData":[OSD([subQ0]),TDD([makeQuery(id+"F2.imprint","IMPRINT",EDGE,{"disambiguationData":[TD([[makeQuery(id+"F2.imprint","INTERSECT",VERTEX,{"derivedFrom":[subQ0,sQuery(id+"F2.wireOp",EDGE,"E13.1.2")]}),-1.0]])],"derivedFrom":subQ0})])],"isStart":true});}
            var Q78;
            Q78=makeQuery(id+"F3.opExtrude","CAP_EDGE",EDGE,{"disambiguationData":[OSD([sQuery(id+"F2.wireOp",EDGE,"E13.1.0")])],"isStart":true});
            var Q79;
            {var subQ0=sQuery(id+"F2.wireOp",EDGE,"E0");Q79=makeQuery(id+"F3.opExtrude","CAP_EDGE",EDGE,{"disambiguationData":[OSD([subQ0]),TDD([makeQuery(id+"F2.imprint","IMPRINT",EDGE,{"disambiguationData":[TD([[makeQuery(id+"F2.imprint","INTERSECT",VERTEX,{"derivedFrom":[subQ0,sQuery(id+"F2.wireOp",EDGE,"E11.MirrorCS")]}),-1.0]])],"derivedFrom":subQ0})])],"isStart":true});}
            var Q80;
            Q80=makeQuery(id+"F3.opExtrude","CAP_EDGE",EDGE,{"disambiguationData":[OSD([sQuery(id+"F2.wireOp",EDGE,"E11.MirrorCS")])],"isStart":true});
            var Q81;
            Q81=makeQuery(id+"F3.opExtrude","CAP_EDGE",EDGE,{"disambiguationData":[OSD([sQuery(id+"F2.wireOp",EDGE,"E10.trimOffspring")])],"isStart":true});
            var Q82;
            {var subQ0=sQuery(id+"F2.wireOp",EDGE,"E0");Q82=makeQuery(id+"F3.opExtrude","CAP_EDGE",EDGE,{"disambiguationData":[OSD([subQ0]),TDD([makeQuery(id+"F2.imprint","IMPRINT",EDGE,{"disambiguationData":[TD([[makeQuery(id+"F2.imprint","INTERSECT",VERTEX,{"derivedFrom":[subQ0,sQuery(id+"F2.wireOp",EDGE,"E10.trimOffspring")]}),1.0]])],"derivedFrom":subQ0})])],"isStart":true});}
            var Q83;
            Q83=makeQuery(id+"F3.opExtrude","CAP_EDGE",EDGE,{"disambiguationData":[OSD([sQuery(id+"F2.wireOp",EDGE,"E13.19.2")])],"isStart":true});
            var Q84;
            Q84=makeQuery(id+"F3.opExtrude","CAP_EDGE",EDGE,{"disambiguationData":[OSD([sQuery(id+"F2.wireOp",EDGE,"E13.19.0")])],"isStart":true});
            var Q85;
            {var subQ0=sQuery(id+"F2.wireOp",EDGE,"E0");Q85=makeQuery(id+"F3.opExtrude","CAP_EDGE",EDGE,{"disambiguationData":[OSD([subQ0]),TDD([makeQuery(id+"F2.imprint","IMPRINT",EDGE,{"disambiguationData":[TD([[makeQuery(id+"F2.imprint","INTERSECT",VERTEX,{"derivedFrom":[subQ0,sQuery(id+"F2.wireOp",EDGE,"E13.18.2")]}),-1.0]])],"derivedFrom":subQ0})])],"isStart":true});}
            var Q86;
            Q86=makeQuery(id+"F3.opExtrude","CAP_EDGE",EDGE,{"disambiguationData":[OSD([sQuery(id+"F2.wireOp",EDGE,"E13.18.2")])],"isStart":true});
            var Q87;
            Q87=makeQuery(id+"F3.opExtrude","CAP_EDGE",EDGE,{"disambiguationData":[OSD([sQuery(id+"F2.wireOp",EDGE,"E13.18.0")])],"isStart":true});
            var Q88;
            {var subQ0=sQuery(id+"F2.wireOp",EDGE,"E0");Q88=makeQuery(id+"F3.opExtrude","CAP_EDGE",EDGE,{"disambiguationData":[OSD([subQ0]),TDD([makeQuery(id+"F2.imprint","IMPRINT",EDGE,{"disambiguationData":[TD([[makeQuery(id+"F2.imprint","INTERSECT",VERTEX,{"derivedFrom":[subQ0,sQuery(id+"F2.wireOp",EDGE,"E13.17.2")]}),-1.0]])],"derivedFrom":subQ0})])],"isStart":true});}
            var Q89;
            Q89=makeQuery(id+"F3.opExtrude","CAP_EDGE",EDGE,{"disambiguationData":[OSD([sQuery(id+"F2.wireOp",EDGE,"E13.17.2")])],"isStart":true});
            var Q90;
            Q90=makeQuery(id+"F3.opExtrude","CAP_EDGE",EDGE,{"disambiguationData":[OSD([sQuery(id+"F2.wireOp",EDGE,"E13.17.0")])],"isStart":true});
            var Q91;
            {var subQ0=sQuery(id+"F2.wireOp",EDGE,"E0");Q91=makeQuery(id+"F3.opExtrude","CAP_EDGE",EDGE,{"disambiguationData":[OSD([subQ0]),TDD([makeQuery(id+"F2.imprint","IMPRINT",EDGE,{"disambiguationData":[TD([[makeQuery(id+"F2.imprint","INTERSECT",VERTEX,{"derivedFrom":[subQ0,sQuery(id+"F2.wireOp",EDGE,"E13.16.2")]}),-1.0]])],"derivedFrom":subQ0})])],"isStart":true});}
            var Q92;
            Q92=makeQuery(id+"F3.opExtrude","CAP_EDGE",EDGE,{"disambiguationData":[OSD([sQuery(id+"F2.wireOp",EDGE,"E13.16.2")])],"isStart":true});
            var Q93;
            Q93=makeQuery(id+"F3.opExtrude","CAP_EDGE",EDGE,{"disambiguationData":[OSD([sQuery(id+"F2.wireOp",EDGE,"E13.16.0")])],"isStart":true});
            var Q94;
            {var subQ0=sQuery(id+"F2.wireOp",EDGE,"E0");Q94=makeQuery(id+"F3.opExtrude","CAP_EDGE",EDGE,{"disambiguationData":[OSD([subQ0]),TDD([makeQuery(id+"F2.imprint","IMPRINT",EDGE,{"disambiguationData":[TD([[makeQuery(id+"F2.imprint","INTERSECT",VERTEX,{"derivedFrom":[subQ0,sQuery(id+"F2.wireOp",EDGE,"E13.15.2")]}),-1.0]])],"derivedFrom":subQ0})])],"isStart":true});}
            var Q95;
            Q95=makeQuery(id+"F3.opExtrude","CAP_EDGE",EDGE,{"disambiguationData":[OSD([sQuery(id+"F2.wireOp",EDGE,"E13.15.2")])],"isStart":true});
            var Q96;
            Q96=makeQuery(id+"F3.opExtrude","CAP_EDGE",EDGE,{"disambiguationData":[OSD([sQuery(id+"F2.wireOp",EDGE,"E13.15.0")])],"isStart":true});
            var Q97;
            {var subQ0=sQuery(id+"F2.wireOp",EDGE,"E0");Q97=makeQuery(id+"F3.opExtrude","CAP_EDGE",EDGE,{"disambiguationData":[OSD([subQ0]),TDD([makeQuery(id+"F2.imprint","IMPRINT",EDGE,{"disambiguationData":[TD([[makeQuery(id+"F2.imprint","INTERSECT",VERTEX,{"derivedFrom":[subQ0,sQuery(id+"F2.wireOp",EDGE,"E13.14.2")]}),-1.0]])],"derivedFrom":subQ0})])],"isStart":true});}
            var Q98;
            Q98=makeQuery(id+"F3.opExtrude","CAP_EDGE",EDGE,{"disambiguationData":[OSD([sQuery(id+"F2.wireOp",EDGE,"E13.14.2")])],"isStart":true});
            var Q99;
            Q99=makeQuery(id+"F3.opExtrude","CAP_EDGE",EDGE,{"disambiguationData":[OSD([sQuery(id+"F2.wireOp",EDGE,"E13.14.0")])],"isStart":true});
            var Q100;
            {var subQ0=sQuery(id+"F2.wireOp",EDGE,"E0");Q100=makeQuery(id+"F3.opExtrude","CAP_EDGE",EDGE,{"disambiguationData":[OSD([subQ0]),TDD([makeQuery(id+"F2.imprint","IMPRINT",EDGE,{"disambiguationData":[TD([[makeQuery(id+"F2.imprint","INTERSECT",VERTEX,{"derivedFrom":[subQ0,sQuery(id+"F2.wireOp",EDGE,"E13.13.2")]}),-1.0]])],"derivedFrom":subQ0})])],"isStart":true});}
            var Q101;
            Q101=makeQuery(id+"F3.opExtrude","CAP_EDGE",EDGE,{"disambiguationData":[OSD([sQuery(id+"F2.wireOp",EDGE,"E13.13.2")])],"isStart":true});
            var Q102;
            Q102=makeQuery(id+"F3.opExtrude","CAP_EDGE",EDGE,{"disambiguationData":[OSD([sQuery(id+"F2.wireOp",EDGE,"E13.13.0")])],"isStart":true});
            var Q103;
            {var subQ0=sQuery(id+"F2.wireOp",EDGE,"E0");Q103=makeQuery(id+"F3.opExtrude","CAP_EDGE",EDGE,{"disambiguationData":[OSD([subQ0]),TDD([makeQuery(id+"F2.imprint","IMPRINT",EDGE,{"disambiguationData":[TD([[makeQuery(id+"F2.imprint","INTERSECT",VERTEX,{"derivedFrom":[subQ0,sQuery(id+"F2.wireOp",EDGE,"E13.12.2")]}),-1.0]])],"derivedFrom":subQ0})])],"isStart":true});}
            var Q104;
            Q104=makeQuery(id+"F3.opExtrude","CAP_EDGE",EDGE,{"disambiguationData":[OSD([sQuery(id+"F2.wireOp",EDGE,"E13.12.2")])],"isStart":true});
            var Q105;
            Q105=makeQuery(id+"F3.opExtrude","CAP_EDGE",EDGE,{"disambiguationData":[OSD([sQuery(id+"F2.wireOp",EDGE,"E13.12.0")])],"isStart":true});
            var Q106;
            {var subQ0=sQuery(id+"F2.wireOp",EDGE,"E0");Q106=makeQuery(id+"F3.opExtrude","CAP_EDGE",EDGE,{"disambiguationData":[OSD([subQ0]),TDD([makeQuery(id+"F2.imprint","IMPRINT",EDGE,{"disambiguationData":[TD([[makeQuery(id+"F2.imprint","INTERSECT",VERTEX,{"derivedFrom":[subQ0,sQuery(id+"F2.wireOp",EDGE,"E13.11.2")]}),-1.0]])],"derivedFrom":subQ0})])],"isStart":true});}
            var Q107;
            Q107=makeQuery(id+"F3.opExtrude","CAP_EDGE",EDGE,{"disambiguationData":[OSD([sQuery(id+"F2.wireOp",EDGE,"E13.11.2")])],"isStart":true});
            var Q108;
            Q108=makeQuery(id+"F3.opExtrude","CAP_EDGE",EDGE,{"disambiguationData":[OSD([sQuery(id+"F2.wireOp",EDGE,"E13.11.0")])],"isStart":true});
            var Q109;
            {var subQ0=sQuery(id+"F2.wireOp",EDGE,"E0");Q109=makeQuery(id+"F3.opExtrude","CAP_EDGE",EDGE,{"disambiguationData":[OSD([subQ0]),TDD([makeQuery(id+"F2.imprint","IMPRINT",EDGE,{"disambiguationData":[TD([[makeQuery(id+"F2.imprint","INTERSECT",VERTEX,{"derivedFrom":[subQ0,sQuery(id+"F2.wireOp",EDGE,"E13.10.2")]}),-1.0]])],"derivedFrom":subQ0})])],"isStart":true});}
            var Q110;
            Q110=makeQuery(id+"F3.opExtrude","CAP_EDGE",EDGE,{"disambiguationData":[OSD([sQuery(id+"F2.wireOp",EDGE,"E13.10.2")])],"isStart":true});
            var Q111;
            Q111=makeQuery(id+"F3.opExtrude","CAP_EDGE",EDGE,{"disambiguationData":[OSD([sQuery(id+"F2.wireOp",EDGE,"E13.10.0")])],"isStart":true});
            var Q112;
            {var subQ0=sQuery(id+"F2.wireOp",EDGE,"E0");Q112=makeQuery(id+"F3.opExtrude","CAP_EDGE",EDGE,{"disambiguationData":[OSD([subQ0]),TDD([makeQuery(id+"F2.imprint","IMPRINT",EDGE,{"disambiguationData":[TD([[makeQuery(id+"F2.imprint","INTERSECT",VERTEX,{"derivedFrom":[subQ0,sQuery(id+"F2.wireOp",EDGE,"E13.9.2")]}),-1.0]])],"derivedFrom":subQ0})])],"isStart":true});}
            var Q113;
            Q113=makeQuery(id+"F3.opExtrude","CAP_EDGE",EDGE,{"disambiguationData":[OSD([sQuery(id+"F2.wireOp",EDGE,"E13.9.2")])],"isStart":true});
            var Q114;
            Q114=makeQuery(id+"F3.opExtrude","CAP_EDGE",EDGE,{"disambiguationData":[OSD([sQuery(id+"F2.wireOp",EDGE,"E13.9.0")])],"isStart":true});
            var Q115;
            {var subQ0=sQuery(id+"F2.wireOp",EDGE,"E0");Q115=makeQuery(id+"F3.opExtrude","CAP_EDGE",EDGE,{"disambiguationData":[OSD([subQ0]),TDD([makeQuery(id+"F2.imprint","IMPRINT",EDGE,{"disambiguationData":[TD([[makeQuery(id+"F2.imprint","INTERSECT",VERTEX,{"derivedFrom":[subQ0,sQuery(id+"F2.wireOp",EDGE,"E13.8.2")]}),-1.0]])],"derivedFrom":subQ0})])],"isStart":true});}
            var Q116;
            Q116=makeQuery(id+"F3.opExtrude","CAP_EDGE",EDGE,{"disambiguationData":[OSD([sQuery(id+"F2.wireOp",EDGE,"E13.8.2")])],"isStart":true});
            fillet(context, id + "F4", {"entities" : qUnion([Q0, Q1, Q2, Q3, Q4, Q5, Q6, Q7, Q8, Q9, Q10, Q11, Q12, Q13, Q14, Q15, Q16, Q17, Q18, Q19, Q20, Q21, Q22, Q23, Q24, Q25, Q26, Q27, Q28, Q29, Q30, Q31, Q32, Q33, Q34, Q35, Q36, Q37, Q38, Q39, Q40, Q41, Q42, Q43, Q44, Q45, Q46, Q47, Q48, Q49, Q50, Q51, Q52, Q53, Q54, Q55, Q56, Q57, Q58, Q59, Q60, Q61, Q62, Q63, Q64, Q65, Q66, Q67, Q68, Q69, Q70, Q71, Q72, Q73, Q74, Q75, Q76, Q77, Q78, Q79, Q80, Q81, Q82, Q83, Q84, Q85, Q86, Q87, Q88, Q89, Q90, Q91, Q92, Q93, Q94, Q95, Q96, Q97, Q98, Q99, Q100, Q101, Q102, Q103, Q104, Q105, Q106, Q107, Q108, Q109, Q110, Q111, Q112, Q113, Q114, Q115, Q116]), "radius" : (getVariable(context, 'TeethFillet')) * mm, "tangentPropagation" : true, "allowEdgeOverflow" : false});
        }
    });
